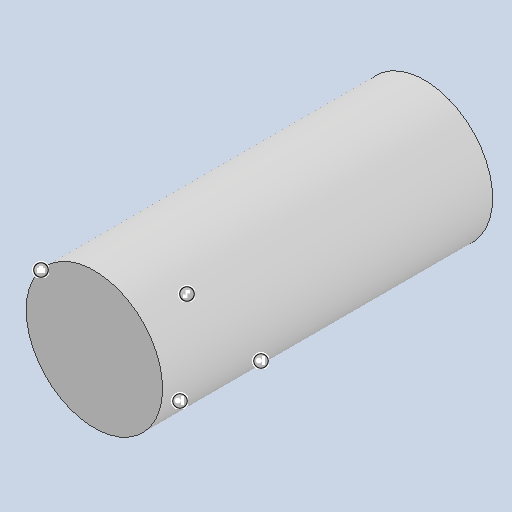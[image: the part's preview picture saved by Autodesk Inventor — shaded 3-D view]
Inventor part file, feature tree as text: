
AUTODESK INVENTOR PART (.ipt)
format: ipt  version: 2025.1 (Build 291241000, 241)  size: 205,312 bytes
history: native  units: mm
features: extrude x1
ambient origin geometry x8: Origin, YZ Plane, XZ Plane, XY Plane, X Axis, Y Axis, Z Axis, Center Point
bodies: Solid1 (feature_tree)
feature tree (1):
  extrude  "Extrusion1"  TaperAngle=0.0deg  [1 undecoded]
note: 1 required parameter value undecoded (feature->parameter linkage not recoverable at this tier; creation-order binding heuristic only, values carry confidence <= 0.55)
